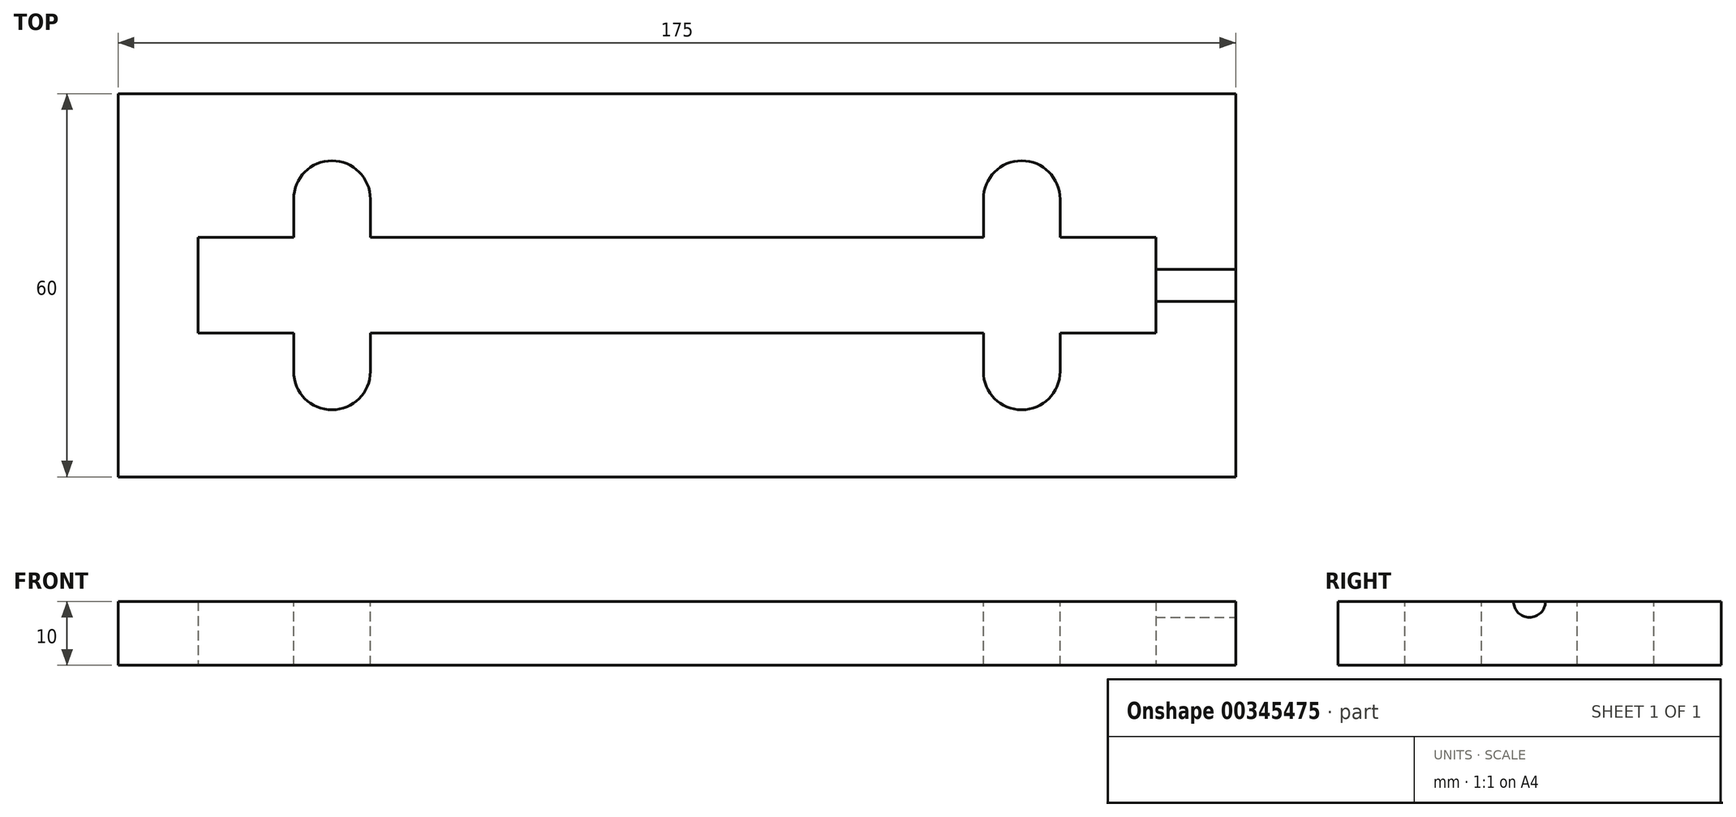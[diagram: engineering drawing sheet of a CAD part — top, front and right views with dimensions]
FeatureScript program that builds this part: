
annotation { "Feature Type Name" : "Feature", "Feature Type Description" : "" }
export const myFeature = defineFeature(function(context is Context, id is Id, definition is map)
    precondition{}
    {
        {
            var Q0;
            Q0=qCreatedBy(makeId("Top.planeOp"),FACE);
            var sketch = newSketch(context, id + "F0", { "sketchPlane" : qUnion([Q0])});
            skLineSegment(sketch, "E0.bottom", {"start": v(-46.9, 33.4) * mm, "end": v(128.1, 33.4) * mm});
            skLineSegment(sketch, "E0.top", {"start": v(-46.9, -26.6) * mm, "end": v(128.1, -26.6) * mm});
            skLineSegment(sketch, "E0.left", {"start": v(-46.9, 33.4) * mm, "end": v(-46.9, -26.6) * mm});
            skLineSegment(sketch, "E0.right", {"start": v(128.1, 33.4) * mm, "end": v(128.1, -26.6) * mm});
            skLineSegment(sketch, "E1.bottom", {"start": v(-34.4, 10.9) * mm, "end": v(115.6, 10.9) * mm});
            skLineSegment(sketch, "E1.top", {"start": v(-34.4, -4.1) * mm, "end": v(115.6, -4.1) * mm});
            skLineSegment(sketch, "E1.left", {"start": v(-34.4, 10.9) * mm, "end": v(-34.4, -4.1) * mm});
            skLineSegment(sketch, "E1.right", {"start": v(115.6, 10.9) * mm, "end": v(115.6, -4.1) * mm});
            skSolve(sketch);
        }
        {
            var Q0;
            Q0=makeQuery(id+"F0.imprint","IMPRINT",FACE,{"disambiguationData":[TD([[makeQuery(id+"F0.imprint","IMPRINT",EDGE,{"derivedFrom":sQuery(id+"F0.wireOp",EDGE,"E0.bottom")}),-1.0]])]});
            extrude(context, id + "F1", {"entities" : qUnion([Q0]), "depth" : 10 * mm});
        }
        {
            var Q0;
            Q0=makeQuery(id+"F1.opExtrude","SWEPT_FACE",FACE,{"disambiguationData":[OSD([sQuery(id+"F0.wireOp",EDGE,"E0.right")])]});
            var sketch = newSketch(context, id + "F2", { "sketchPlane" : qUnion([Q0])});
            skCircle(sketch, "E2", {"center": v(3.4, 10) * mm, "radius": 2.5 * mm});
            skSolve(sketch);
        }
        {
            var Q0;
            {var subQ0=sQuery(id+"F2.wireOp",EDGE,"E2");var subQ1=makeQuery(id+"F1.opExtrude","CAP_EDGE",EDGE,{"disambiguationData":[OSD([sQuery(id+"F0.wireOp",EDGE,"E0.right")])],"isStart":false});var subQ2=makeQuery(id+"F2.imprint","INTERSECT",VERTEX,{"disambiguationData":[OD(0.0)],"derivedFrom":[subQ1,subQ0]});Q0=makeQuery(id+"F2.imprint","IMPRINT",FACE,{"disambiguationData":[TD([[makeQuery(id+"F2.imprint","IMPRINT",EDGE,{"disambiguationData":[TD([[subQ2,1.0]])],"derivedFrom":subQ0}),1.0]])]});}
            extrude(context, id + "F3", {"entities" : qUnion([Q0]), "operationType" : NewBodyOperationType.REMOVE, "oppositeDirection" : true, "depth" : 25 * mm});
        }
        {
            var Q0;
            Q0=makeQuery(id+"F1.opExtrude","CAP_FACE",FACE,{"disambiguationData":[OSD([sQuery(id+"F0.wireOp",EDGE,"E0.bottom"),sQuery(id+"F0.wireOp",EDGE,"E0.top"),sQuery(id+"F0.wireOp",EDGE,"E0.left"),sQuery(id+"F0.wireOp",EDGE,"E0.right"),sQuery(id+"F0.wireOp",EDGE,"E1.bottom"),sQuery(id+"F0.wireOp",EDGE,"E1.top"),sQuery(id+"F0.wireOp",EDGE,"E1.left"),sQuery(id+"F0.wireOp",EDGE,"E1.right")])],"isStart":false});
            var sketch = newSketch(context, id + "F4", { "sketchPlane" : qUnion([Q0])});
            skLineSegment(sketch, "E3.bottom", {"start": v(-19.4, 16.9) * mm, "end": v(-7.4, 16.9) * mm});
            skLineSegment(sketch, "E3.top", {"start": v(-19.4, -10.1) * mm, "end": v(-7.4, -10.1) * mm});
            skLineSegment(sketch, "E3.left", {"start": v(-19.4, 16.9) * mm, "end": v(-19.4, -10.1) * mm});
            skLineSegment(sketch, "E3.right", {"start": v(-7.4, 16.9) * mm, "end": v(-7.4, -10.1) * mm});
            skLineSegment(sketch, "E4.bottom", {"start": v(88.6, 16.9) * mm, "end": v(100.6, 16.9) * mm});
            skLineSegment(sketch, "E4.top", {"start": v(88.6, -10.1) * mm, "end": v(100.6, -10.1) * mm});
            skLineSegment(sketch, "E4.left", {"start": v(88.6, 16.9) * mm, "end": v(88.6, -10.1) * mm});
            skLineSegment(sketch, "E4.right", {"start": v(100.6, 16.9) * mm, "end": v(100.6, -10.1) * mm});
            skCircle(sketch, "E5", {"center": v(-13.4, 16.9) * mm, "radius": 6 * mm});
            skCircle(sketch, "E6", {"center": v(94.6, 16.9) * mm, "radius": 6 * mm});
            skCircle(sketch, "E7", {"center": v(94.6, -10.1) * mm, "radius": 6 * mm});
            skCircle(sketch, "E8", {"center": v(-13.4, -10.1) * mm, "radius": 6 * mm});
            skSolve(sketch);
        }
        {
            var Q0;
            {var subQ0=sQuery(id+"F4.wireOp",EDGE,"E3.bottom");Q0=makeQuery(id+"F4.imprint","IMPRINT",FACE,{"disambiguationData":[TD([[makeQuery(id+"F4.imprint","IMPRINT",EDGE,{"derivedFrom":subQ0}),-1.0]])]});}
            var Q1;
            {var subQ1=makeQuery(id+"F1.opExtrude","CAP_EDGE",EDGE,{"disambiguationData":[OSD([sQuery(id+"F0.wireOp",EDGE,"E1.bottom")])],"isStart":false});var subQ7=sQuery(id+"F4.wireOp",EDGE,"E3.left");var subQ8=makeQuery(id+"F4.imprint","INTERSECT",VERTEX,{"derivedFrom":[subQ1,subQ7]});Q1=makeQuery(id+"F4.imprint","IMPRINT",FACE,{"disambiguationData":[TD([[makeQuery(id+"F4.imprint","IMPRINT",EDGE,{"disambiguationData":[TD([[subQ8,-1.0]])],"derivedFrom":subQ7}),1.0]])]});}
            var Q2;
            {var subQ0=sQuery(id+"F4.wireOp",EDGE,"E3.bottom");Q2=makeQuery(id+"F4.imprint","IMPRINT",FACE,{"disambiguationData":[TD([[makeQuery(id+"F4.imprint","IMPRINT",EDGE,{"derivedFrom":subQ0}),1.0]])]});}
            var Q3;
            {var subQ1=sQuery(id+"F4.wireOp",EDGE,"E3.right");var subQ3=makeQuery(id+"F1.opExtrude","CAP_EDGE",EDGE,{"disambiguationData":[OSD([sQuery(id+"F0.wireOp",EDGE,"E1.bottom")])],"isStart":false});var subQ4=makeQuery(id+"F4.imprint","INTERSECT",VERTEX,{"derivedFrom":[subQ3,subQ1]});Q3=makeQuery(id+"F4.imprint","IMPRINT",FACE,{"disambiguationData":[TD([[makeQuery(id+"F4.imprint","IMPRINT",EDGE,{"disambiguationData":[TD([[subQ4,1.0]])],"derivedFrom":subQ3}),1.0]])]});}
            var Q4;
            {var subQ1=sQuery(id+"F4.wireOp",EDGE,"E3.left");var subQ3=makeQuery(id+"F1.opExtrude","CAP_EDGE",EDGE,{"disambiguationData":[OSD([sQuery(id+"F0.wireOp",EDGE,"E1.bottom")])],"isStart":false});var subQ4=makeQuery(id+"F4.imprint","INTERSECT",VERTEX,{"derivedFrom":[subQ3,subQ1]});Q4=makeQuery(id+"F4.imprint","IMPRINT",FACE,{"disambiguationData":[TD([[makeQuery(id+"F4.imprint","IMPRINT",EDGE,{"disambiguationData":[TD([[subQ4,-1.0]])],"derivedFrom":subQ3}),1.0]])]});}
            var Q5;
            {var subQ0=sQuery(id+"F4.wireOp",EDGE,"E3.top");Q5=makeQuery(id+"F4.imprint","IMPRINT",FACE,{"disambiguationData":[TD([[makeQuery(id+"F4.imprint","IMPRINT",EDGE,{"derivedFrom":subQ0}),1.0]])]});}
            var Q6;
            {var subQ1=sQuery(id+"F4.wireOp",EDGE,"E3.left");var subQ3=makeQuery(id+"F1.opExtrude","CAP_EDGE",EDGE,{"disambiguationData":[OSD([sQuery(id+"F0.wireOp",EDGE,"E1.top")])],"isStart":false});var subQ4=makeQuery(id+"F4.imprint","INTERSECT",VERTEX,{"derivedFrom":[subQ3,subQ1]});Q6=makeQuery(id+"F4.imprint","IMPRINT",FACE,{"disambiguationData":[TD([[makeQuery(id+"F4.imprint","IMPRINT",EDGE,{"disambiguationData":[TD([[subQ4,-1.0]])],"derivedFrom":subQ3}),-1.0]])]});}
            var Q7;
            {var subQ1=sQuery(id+"F4.wireOp",EDGE,"E3.right");var subQ3=makeQuery(id+"F1.opExtrude","CAP_EDGE",EDGE,{"disambiguationData":[OSD([sQuery(id+"F0.wireOp",EDGE,"E1.top")])],"isStart":false});var subQ4=makeQuery(id+"F4.imprint","INTERSECT",VERTEX,{"derivedFrom":[subQ3,subQ1]});Q7=makeQuery(id+"F4.imprint","IMPRINT",FACE,{"disambiguationData":[TD([[makeQuery(id+"F4.imprint","IMPRINT",EDGE,{"disambiguationData":[TD([[subQ4,1.0]])],"derivedFrom":subQ3}),-1.0]])]});}
            var Q8;
            {var subQ0=sQuery(id+"F4.wireOp",EDGE,"E3.top");Q8=makeQuery(id+"F4.imprint","IMPRINT",FACE,{"disambiguationData":[TD([[makeQuery(id+"F4.imprint","IMPRINT",EDGE,{"derivedFrom":subQ0}),-1.0]])]});}
            var Q9;
            {var subQ0=sQuery(id+"F4.wireOp",EDGE,"E4.top");Q9=makeQuery(id+"F4.imprint","IMPRINT",FACE,{"disambiguationData":[TD([[makeQuery(id+"F4.imprint","IMPRINT",EDGE,{"derivedFrom":subQ0}),-1.0]])]});}
            var Q10;
            {var subQ0=sQuery(id+"F4.wireOp",EDGE,"E4.top");Q10=makeQuery(id+"F4.imprint","IMPRINT",FACE,{"disambiguationData":[TD([[makeQuery(id+"F4.imprint","IMPRINT",EDGE,{"derivedFrom":subQ0}),1.0]])]});}
            var Q11;
            {var subQ1=makeQuery(id+"F1.opExtrude","CAP_EDGE",EDGE,{"disambiguationData":[OSD([sQuery(id+"F0.wireOp",EDGE,"E1.bottom")])],"isStart":false});var subQ7=sQuery(id+"F4.wireOp",EDGE,"E4.left");var subQ8=makeQuery(id+"F4.imprint","INTERSECT",VERTEX,{"derivedFrom":[subQ1,subQ7]});Q11=makeQuery(id+"F4.imprint","IMPRINT",FACE,{"disambiguationData":[TD([[makeQuery(id+"F4.imprint","IMPRINT",EDGE,{"disambiguationData":[TD([[subQ8,-1.0]])],"derivedFrom":subQ7}),1.0]])]});}
            var Q12;
            {var subQ0=sQuery(id+"F4.wireOp",EDGE,"E4.bottom");Q12=makeQuery(id+"F4.imprint","IMPRINT",FACE,{"disambiguationData":[TD([[makeQuery(id+"F4.imprint","IMPRINT",EDGE,{"derivedFrom":subQ0}),-1.0]])]});}
            var Q13;
            {var subQ0=sQuery(id+"F4.wireOp",EDGE,"E4.bottom");Q13=makeQuery(id+"F4.imprint","IMPRINT",FACE,{"disambiguationData":[TD([[makeQuery(id+"F4.imprint","IMPRINT",EDGE,{"derivedFrom":subQ0}),1.0]])]});}
            var Q14;
            {var subQ1=sQuery(id+"F4.wireOp",EDGE,"E4.right");var subQ3=makeQuery(id+"F1.opExtrude","CAP_EDGE",EDGE,{"disambiguationData":[OSD([sQuery(id+"F0.wireOp",EDGE,"E1.bottom")])],"isStart":false});var subQ4=makeQuery(id+"F4.imprint","INTERSECT",VERTEX,{"derivedFrom":[subQ3,subQ1]});Q14=makeQuery(id+"F4.imprint","IMPRINT",FACE,{"disambiguationData":[TD([[makeQuery(id+"F4.imprint","IMPRINT",EDGE,{"disambiguationData":[TD([[subQ4,1.0]])],"derivedFrom":subQ3}),1.0]])]});}
            var Q15;
            {var subQ1=sQuery(id+"F4.wireOp",EDGE,"E4.left");var subQ3=makeQuery(id+"F1.opExtrude","CAP_EDGE",EDGE,{"disambiguationData":[OSD([sQuery(id+"F0.wireOp",EDGE,"E1.bottom")])],"isStart":false});var subQ4=makeQuery(id+"F4.imprint","INTERSECT",VERTEX,{"derivedFrom":[subQ3,subQ1]});Q15=makeQuery(id+"F4.imprint","IMPRINT",FACE,{"disambiguationData":[TD([[makeQuery(id+"F4.imprint","IMPRINT",EDGE,{"disambiguationData":[TD([[subQ4,-1.0]])],"derivedFrom":subQ3}),1.0]])]});}
            var Q16;
            {var subQ1=sQuery(id+"F4.wireOp",EDGE,"E4.left");var subQ3=makeQuery(id+"F1.opExtrude","CAP_EDGE",EDGE,{"disambiguationData":[OSD([sQuery(id+"F0.wireOp",EDGE,"E1.top")])],"isStart":false});var subQ4=makeQuery(id+"F4.imprint","INTERSECT",VERTEX,{"derivedFrom":[subQ3,subQ1]});Q16=makeQuery(id+"F4.imprint","IMPRINT",FACE,{"disambiguationData":[TD([[makeQuery(id+"F4.imprint","IMPRINT",EDGE,{"disambiguationData":[TD([[subQ4,-1.0]])],"derivedFrom":subQ3}),-1.0]])]});}
            var Q17;
            {var subQ1=sQuery(id+"F4.wireOp",EDGE,"E4.right");var subQ3=makeQuery(id+"F1.opExtrude","CAP_EDGE",EDGE,{"disambiguationData":[OSD([sQuery(id+"F0.wireOp",EDGE,"E1.top")])],"isStart":false});var subQ4=makeQuery(id+"F4.imprint","INTERSECT",VERTEX,{"derivedFrom":[subQ3,subQ1]});Q17=makeQuery(id+"F4.imprint","IMPRINT",FACE,{"disambiguationData":[TD([[makeQuery(id+"F4.imprint","IMPRINT",EDGE,{"disambiguationData":[TD([[subQ4,1.0]])],"derivedFrom":subQ3}),-1.0]])]});}
            extrude(context, id + "F5", {"entities" : qUnion([Q0, Q1, Q2, Q3, Q4, Q5, Q6, Q7, Q8, Q9, Q10, Q11, Q12, Q13, Q14, Q15, Q16, Q17]), "operationType" : NewBodyOperationType.REMOVE, "oppositeDirection" : true, "depth" : 25 * mm});
        }
    });
